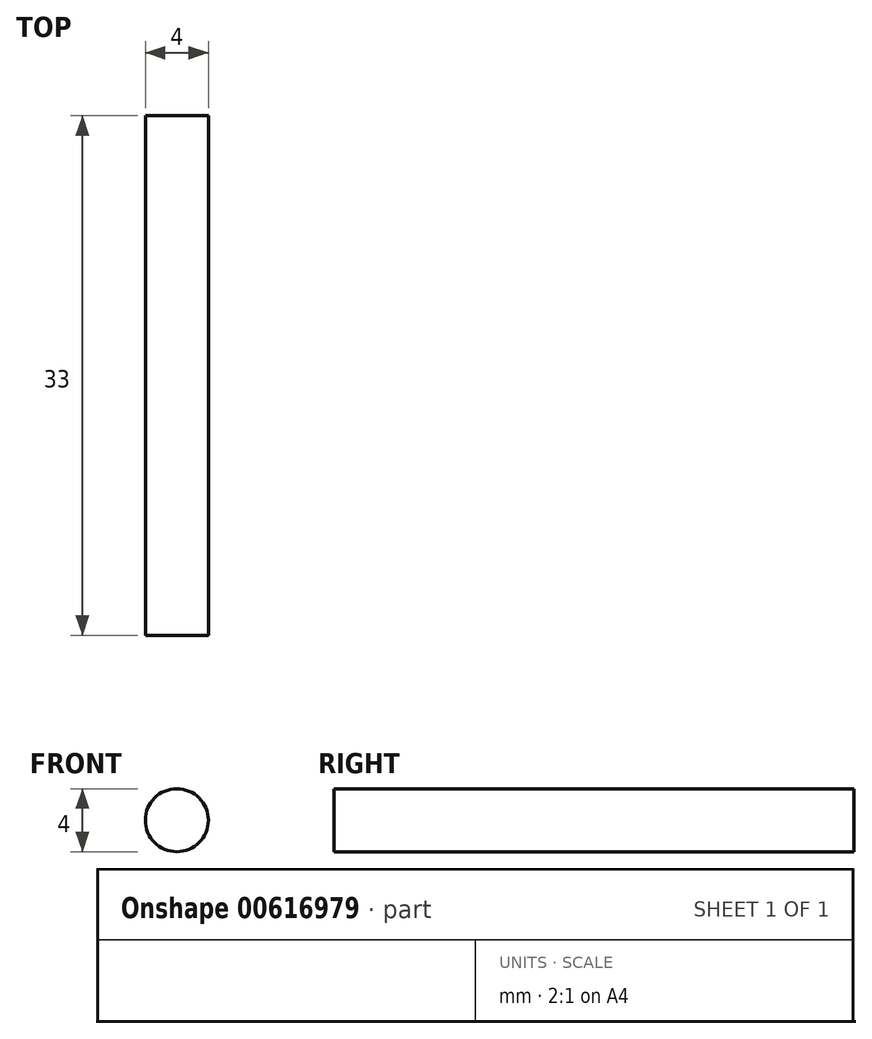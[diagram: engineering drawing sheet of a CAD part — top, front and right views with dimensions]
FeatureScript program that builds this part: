
annotation { "Feature Type Name" : "Feature", "Feature Type Description" : "" }
export const myFeature = defineFeature(function(context is Context, id is Id, definition is map)
    precondition{}
    {
        {
            var Q0;
            Q0=qCreatedBy(makeId("Front.planeOp"),FACE);
            var sketch = newSketch(context, id + "F0", { "sketchPlane" : qUnion([Q0])});
            skCircle(sketch, "E0", {"center": v(0, 0) * mm, "radius": 2 * mm});
            skSolve(sketch);
        }
        {
            var Q0;
            Q0=makeQuery(id+"F0.imprint","IMPRINT",FACE,{"disambiguationData":[TD([[makeQuery(id+"F0.imprint","IMPRINT",EDGE,{"derivedFrom":sQuery(id+"F0.wireOp",EDGE,"E0")}),1.0]])]});
            extrude(context, id + "F1", {"entities" : qUnion([Q0]), "depth" : 33 * mm, "offsetDistance" : 25 * mm});
        }
    });
